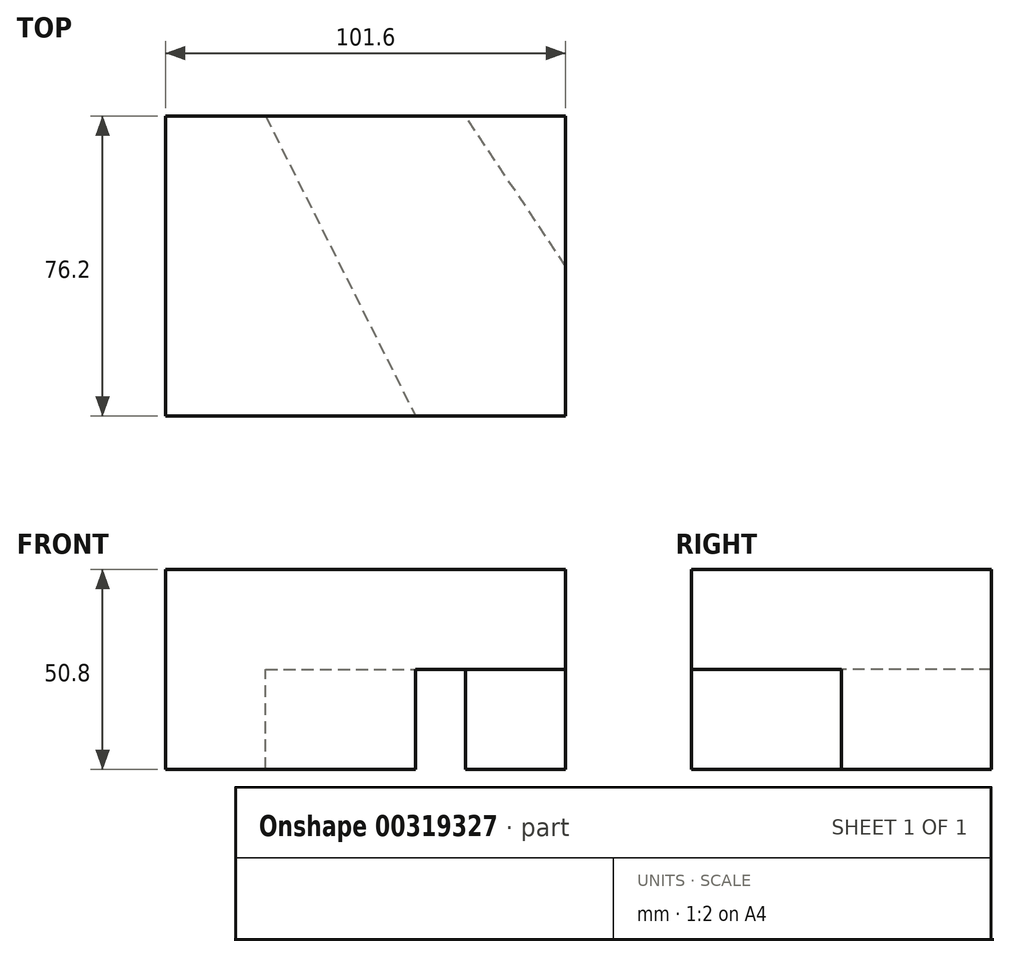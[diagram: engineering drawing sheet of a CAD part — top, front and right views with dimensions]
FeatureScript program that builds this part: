
annotation { "Feature Type Name" : "Feature", "Feature Type Description" : "" }
export const myFeature = defineFeature(function(context is Context, id is Id, definition is map)
    precondition{}
    {
        {
            var Q0;
            Q0=qCreatedBy(makeId("Front.planeOp"),FACE);
            var sketch = newSketch(context, id + "F0", { "sketchPlane" : qUnion([Q0])});
            skLineSegment(sketch, "E0", {"start": v(-46.62, -36.6) * mm, "end": v(54.98, -36.6) * mm});
            skLineSegment(sketch, "E1", {"start": v(54.98, -36.6) * mm, "end": v(54.98, -11.2) * mm});
            skLineSegment(sketch, "E2", {"start": v(54.98, -11.2) * mm, "end": v(-46.62, -11.2) * mm});
            skLineSegment(sketch, "E3", {"start": v(-46.62, -11.2) * mm, "end": v(-46.62, -36.6) * mm});
            skSolve(sketch);
        }
        {
            var Q0;
            Q0 = qSketchRegion(id + "F0", true);
            var Q1;
            Q1=makeQuery(id+"F0.imprint","IMPRINT",FACE,{"disambiguationData":[TD([[makeQuery(id+"F0.imprint","IMPRINT",EDGE,{"derivedFrom":sQuery(id+"F0.wireOp",EDGE,"E0")}),1.0]])]});
            extrude(context, id + "F1", {"entities" : qUnion([Q0, Q1]), "depth" : 76.2 * mm});
        }
        {
            var Q0;
            Q0=makeQuery(id+"F1.opExtrude","SWEPT_FACE",FACE,{"disambiguationData":[OSD([sQuery(id+"F0.wireOp",EDGE,"E0")])]});
            var sketch = newSketch(context, id + "F2", { "sketchPlane" : qUnion([Q0])});
            skLineSegment(sketch, "E4", {"start": v(54.98, 0) * mm, "end": v(29.58, 0) * mm});
            skLineSegment(sketch, "E5", {"start": v(54.98, 0) * mm, "end": v(54.98, 38.1) * mm});
            skLineSegment(sketch, "E6", {"start": v(54.98, 38.1) * mm, "end": v(29.58, 0) * mm});
            skSolve(sketch);
        }
        {
            var Q0;
            Q0=makeQuery(id+"F2.imprint","IMPRINT",FACE,{"disambiguationData":[TD([[makeQuery(id+"F2.imprint","IMPRINT",EDGE,{"derivedFrom":sQuery(id+"F2.wireOp",EDGE,"E4")}),1.0]])]});
            extrude(context, id + "F3", {"entities" : qUnion([Q0]), "operationType" : NewBodyOperationType.ADD, "depth" : 25.4 * mm});
        }
        {
            var Q0;
            Q0=makeQuery(id+"F1.opExtrude","SWEPT_FACE",FACE,{"disambiguationData":[OSD([sQuery(id+"F0.wireOp",EDGE,"E0")])]});
            var sketch = newSketch(context, id + "F4", { "sketchPlane" : qUnion([Q0])});
            skLineSegment(sketch, "E7", {"start": v(-46.62, 0) * mm, "end": v(-21.22, 0) * mm});
            skLineSegment(sketch, "E8", {"start": v(-21.22, 0) * mm, "end": v(16.88, 76.2) * mm});
            skLineSegment(sketch, "E9", {"start": v(16.88, 76.2) * mm, "end": v(-46.62, 76.2) * mm});
            skLineSegment(sketch, "E10", {"start": v(-46.62, 76.2) * mm, "end": v(-46.62, 0) * mm});
            skLineSegment(sketch, "E11", {"start": v(-21.22, 0) * mm, "end": v(-46.62, 0) * mm});
            skSolve(sketch);
        }
        {
            var Q0;
            Q0=makeQuery(id+"F4.imprint","IMPRINT",FACE,{"disambiguationData":[TD([[makeQuery(id+"F4.imprint","IMPRINT",EDGE,{"derivedFrom":sQuery(id+"F4.wireOp",EDGE,"E8")}),1.0]])]});
            extrude(context, id + "F5", {"entities" : qUnion([Q0]), "operationType" : NewBodyOperationType.ADD, "depth" : 25.4 * mm});
        }
    });
